# Revit family: QF_EVEREST_EMGF36
name_source: partatom
category: Specialty Equipment
revit_build: Autodesk Revit 2015 (Build: 20140606_1530(x64)
units: mm (PartAtom-declared; Revit-internal decimal feet)

## types (1)
- EMGF36
    Apparent Power = 0 VA
    BTUH = 5441.0 Btu/h
    Conn Conduit = Yes
    Conn Plug = NEMA 5-20P
    Cycle = 60 Hz
    Depth = 803 mm  [stored 2.63451 ft]
    Description = GLASS DOOR MERCHANDISER FREEZER
    Elec Conn Connection Height = 0 mm  [stored 0 ft]
    Elec Conn RI Height = 0 mm  [stored 0 ft]
    FL Amps = 5 A
    Foodservice Equipment Identifier = Yes
    HP = 1 1/4
    Height = 2130 mm
    Identify Quantity as Lot = Yes
    Length = 1040 mm  [stored 3.41207 ft]
    Manufacturer = EVEREST
    Max Overcurrent Protection = 0 A
    Min Ckt Ampacity = 0 A
    Model = EMGF36
    Number of Poles = 1
    Phase = 1
    Refrigerant Type = R-404A/R-290
    Refrigerant Volume = 0.00 kip
    Volts = 230 V
    Watts = 1242 W
    Weight in Pounds = 592

note: [stored X ft] marks values corroborated as IEEE doubles in the binary element streams (Revit-internal decimal feet)

## geometry (parser evidence)
native form markers: Sweep x3
no freeform markers — native parametric forms only
